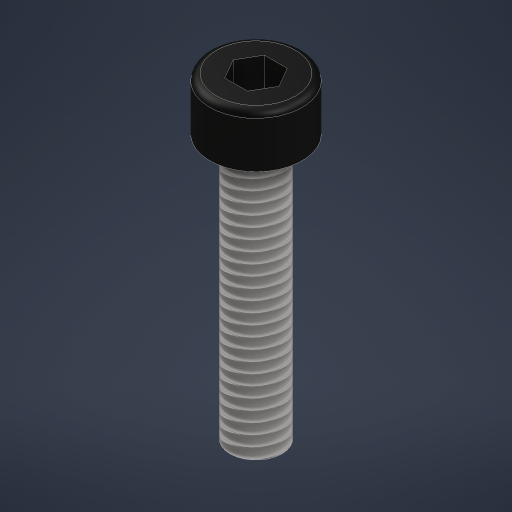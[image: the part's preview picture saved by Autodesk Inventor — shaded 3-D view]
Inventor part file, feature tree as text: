
AUTODESK INVENTOR PART (.ipt)
format: ipt  version: 2024 (Build 280153000, 153)  size: 246,784 bytes
history: native  units: mm
features: extrude x3, sketch x1, fillet x1, thread x1
ambient origin geometry x8: Origin, YZ Plane, XZ Plane, XY Plane, X Axis, Y Axis, Z Axis, Center Point
bodies: Solid1 (feature_tree)
feature tree (6):
  sketch  "Sketch1"  dims[d0=3.94mm d1=7.0mm d2=4.0mm d3=0.0mm d4=20.0mm d5=0.0mm d8=3.0mm d9=3.0mm d10=0.0mm d11=0.5mm d12=20.0mm d13=0.0mm]
  extrude  "Extrusion1"  Depth=20.0mm
  extrude  "Extrusion2"  Depth=4.0mm TaperAngle=0.0deg
  extrude  "Extrusion3"  Depth=20.0mm
  fillet  "Fillet1"  [1 undecoded]
  thread  "Thread2"  [1 undecoded]
note: 2 required parameter values undecoded (feature->parameter linkage not recoverable at this tier; creation-order binding heuristic only, values carry confidence <= 0.55)
